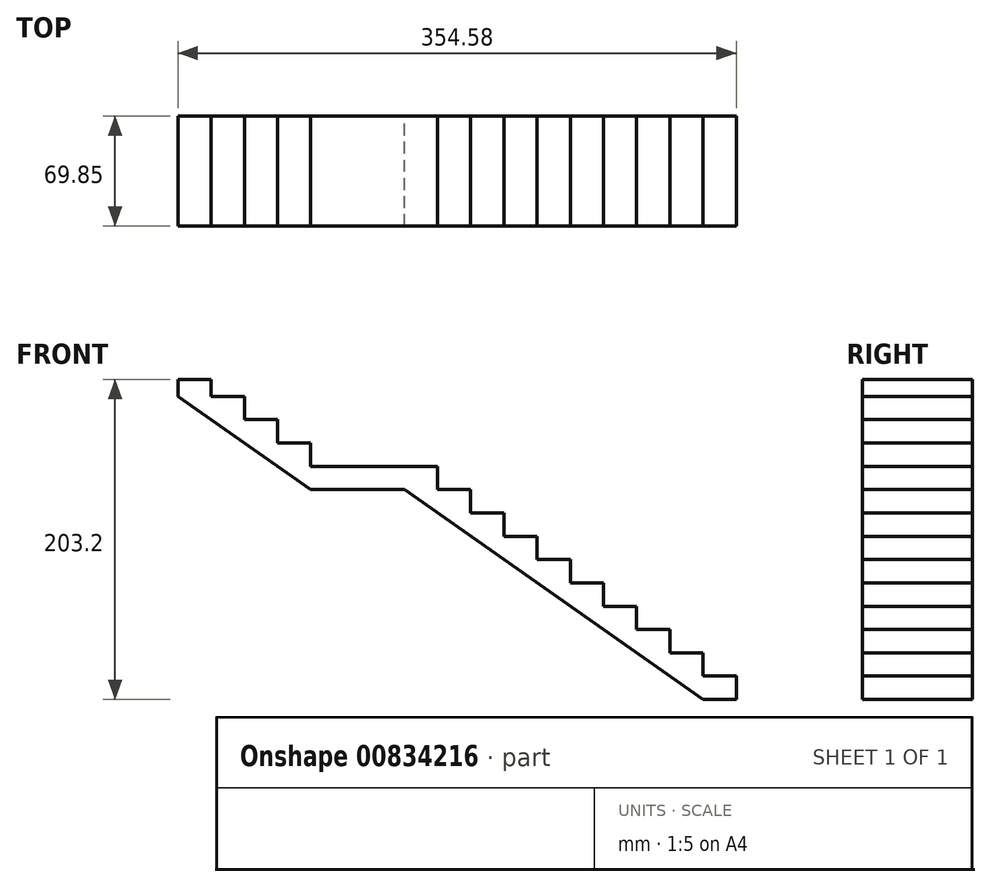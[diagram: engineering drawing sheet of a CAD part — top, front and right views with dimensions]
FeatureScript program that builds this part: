
annotation { "Feature Type Name" : "Feature", "Feature Type Description" : "" }
export const myFeature = defineFeature(function(context is Context, id is Id, definition is map)
    precondition{}
    {
        {
            var Q0;
            Q0=qCreatedBy(makeId("Front.planeOp"),FACE);
            var sketch = newSketch(context, id + "F0", { "sketchPlane" : qUnion([Q0])});
            skLineSegment(sketch, "E0", {"start": v(0, 0) * mm, "end": v(21.08, 0) * mm});
            skLineSegment(sketch, "E1", {"start": v(21.08, 0) * mm, "end": v(21.08, -10.7) * mm});
            skLineSegment(sketch, "E2", {"start": v(21.08, -10.7) * mm, "end": v(42.16, -10.7) * mm});
            skLineSegment(sketch, "E3", {"start": v(42.16, -10.7) * mm, "end": v(42.16, -25.5) * mm});
            skLineSegment(sketch, "E4", {"start": v(42.16, -25.5) * mm, "end": v(63.25, -25.5) * mm});
            skLineSegment(sketch, "E5", {"start": v(63.25, -25.5) * mm, "end": v(63.25, -40.3) * mm});
            skLineSegment(sketch, "E6", {"start": v(63.25, -40.3) * mm, "end": v(84.33, -40.3) * mm});
            skLineSegment(sketch, "E7", {"start": v(84.33, -40.3) * mm, "end": v(84.33, -55.12) * mm});
            skLineSegment(sketch, "E8", {"start": v(84.33, -55.12) * mm, "end": v(164.85, -55.12) * mm});
            skLineSegment(sketch, "E9", {"start": v(164.85, -55.12) * mm, "end": v(164.85, -69.93) * mm});
            skLineSegment(sketch, "E10", {"start": v(164.85, -69.93) * mm, "end": v(185.93, -69.93) * mm});
            skLineSegment(sketch, "E11", {"start": v(185.93, -69.93) * mm, "end": v(185.93, -84.73) * mm});
            skLineSegment(sketch, "E12", {"start": v(185.93, -84.73) * mm, "end": v(207, -84.73) * mm});
            skLineSegment(sketch, "E13", {"start": v(207, -84.73) * mm, "end": v(207, -99.54) * mm});
            skLineSegment(sketch, "E14", {"start": v(207, -99.54) * mm, "end": v(228.1, -99.54) * mm});
            skLineSegment(sketch, "E15", {"start": v(228.1, -99.54) * mm, "end": v(228.1, -114.35) * mm});
            skLineSegment(sketch, "E16", {"start": v(228.1, -114.35) * mm, "end": v(249.17, -114.35) * mm});
            skLineSegment(sketch, "E17", {"start": v(249.17, -114.35) * mm, "end": v(249.17, -129.16) * mm});
            skLineSegment(sketch, "E18", {"start": v(249.17, -129.16) * mm, "end": v(270.26, -129.16) * mm});
            skLineSegment(sketch, "E19", {"start": v(270.26, -129.16) * mm, "end": v(270.26, -143.97) * mm});
            skLineSegment(sketch, "E20", {"start": v(270.26, -143.97) * mm, "end": v(291.34, -143.97) * mm});
            skLineSegment(sketch, "E21", {"start": v(291.34, -143.97) * mm, "end": v(291.34, -158.78) * mm});
            skLineSegment(sketch, "E22", {"start": v(291.34, -158.78) * mm, "end": v(312.42, -158.78) * mm});
            skLineSegment(sketch, "E23", {"start": v(312.42, -158.78) * mm, "end": v(312.42, -173.58) * mm});
            skLineSegment(sketch, "E24", {"start": v(312.42, -173.58) * mm, "end": v(333.5, -173.58) * mm});
            skLineSegment(sketch, "E25", {"start": v(333.5, -173.58) * mm, "end": v(333.5, -188.4) * mm});
            skLineSegment(sketch, "E26", {"start": v(333.5, -188.4) * mm, "end": v(354.58, -188.4) * mm});
            skLineSegment(sketch, "E27", {"start": v(354.58, -188.4) * mm, "end": v(354.58, -203.2) * mm});
            skLineSegment(sketch, "E28", {"start": v(84.33, -69.93) * mm, "end": v(143.76, -69.93) * mm});
            skLineSegment(sketch, "E29", {"start": v(0, 0) * mm, "end": v(0, -10.7) * mm});
            skLineSegment(sketch, "E30", {"start": v(0, -10.7) * mm, "end": v(84.33, -69.93) * mm});
            skLineSegment(sketch, "E31", {"start": v(354.58, -203.2) * mm, "end": v(333.5, -203.2) * mm});
            skPoint(sketch, "E32", {"position": v(143.76, -69.93) * mm});
            skLineSegment(sketch, "E33", {"start": v(333.5, -203.2) * mm, "end": v(143.76, -69.93) * mm});
            skSolve(sketch);
        }
        {
            var Q0;
            Q0=makeQuery(id+"F0.imprint","IMPRINT",FACE,{"disambiguationData":[TD([[makeQuery(id+"F0.imprint","IMPRINT",EDGE,{"derivedFrom":sQuery(id+"F0.wireOp",EDGE,"E0")}),-1.0]])]});
            extrude(context, id + "F1", {"entities" : qUnion([Q0]), "depth" : 69.85 * mm, "offsetDistance" : 25.4 * mm});
        }
    });
